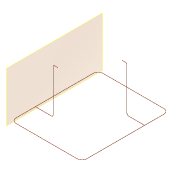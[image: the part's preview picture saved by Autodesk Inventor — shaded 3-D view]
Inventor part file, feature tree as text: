
AUTODESK INVENTOR PART (.ipt)
format: ipt  version: 2016 (Build 200138000, 138)  size: 327,680 bytes
history: native  units: in
note: dims shown in document units (in); Inventor stores cm internally (conversion verified against a paired STEP export)
features: sketch x6, sweep x3, plane x1
ambient origin geometry x8: Origin, YZ Plane, XZ Plane, XY Plane, X Axis, Y Axis, Z Axis, Center Point
bodies: Solid1 (feature_tree)
feature tree (10):
  sweep  "Sweep1"
  sweep  "Sweep3"
  plane  "Work Plane1"
  sweep  "Sweep4"
  sketch  "Sketch1"  dims[d0=0.4291in d1=106.2992in]
  sketch  "Sketch2"  dims[d2=86.6142in d3=6.0in]
  sketch  "Sketch6"  dims[d4=0.0in d11=0.0in]
  sketch  "Sketch7"  dims[d16=21.6535in]
  sketch  "Sketch8"  dims[d17=180.0deg]
  sketch  "Sketch9"  dims[d18=55.1181in d19=90.0deg d20=5.9055in d21=90.0deg d22=1.9685in d23=0.0in d24=0.0in d26=21.6535in d27=0.0in d28=55.1181in d29=90.0deg d30=5.9055in d31=90.0deg d32=1.9685in d33=0.0in d34=0.0in d35=0.4291in d36=23.622in d37=0.4291in d38=23.622in]
